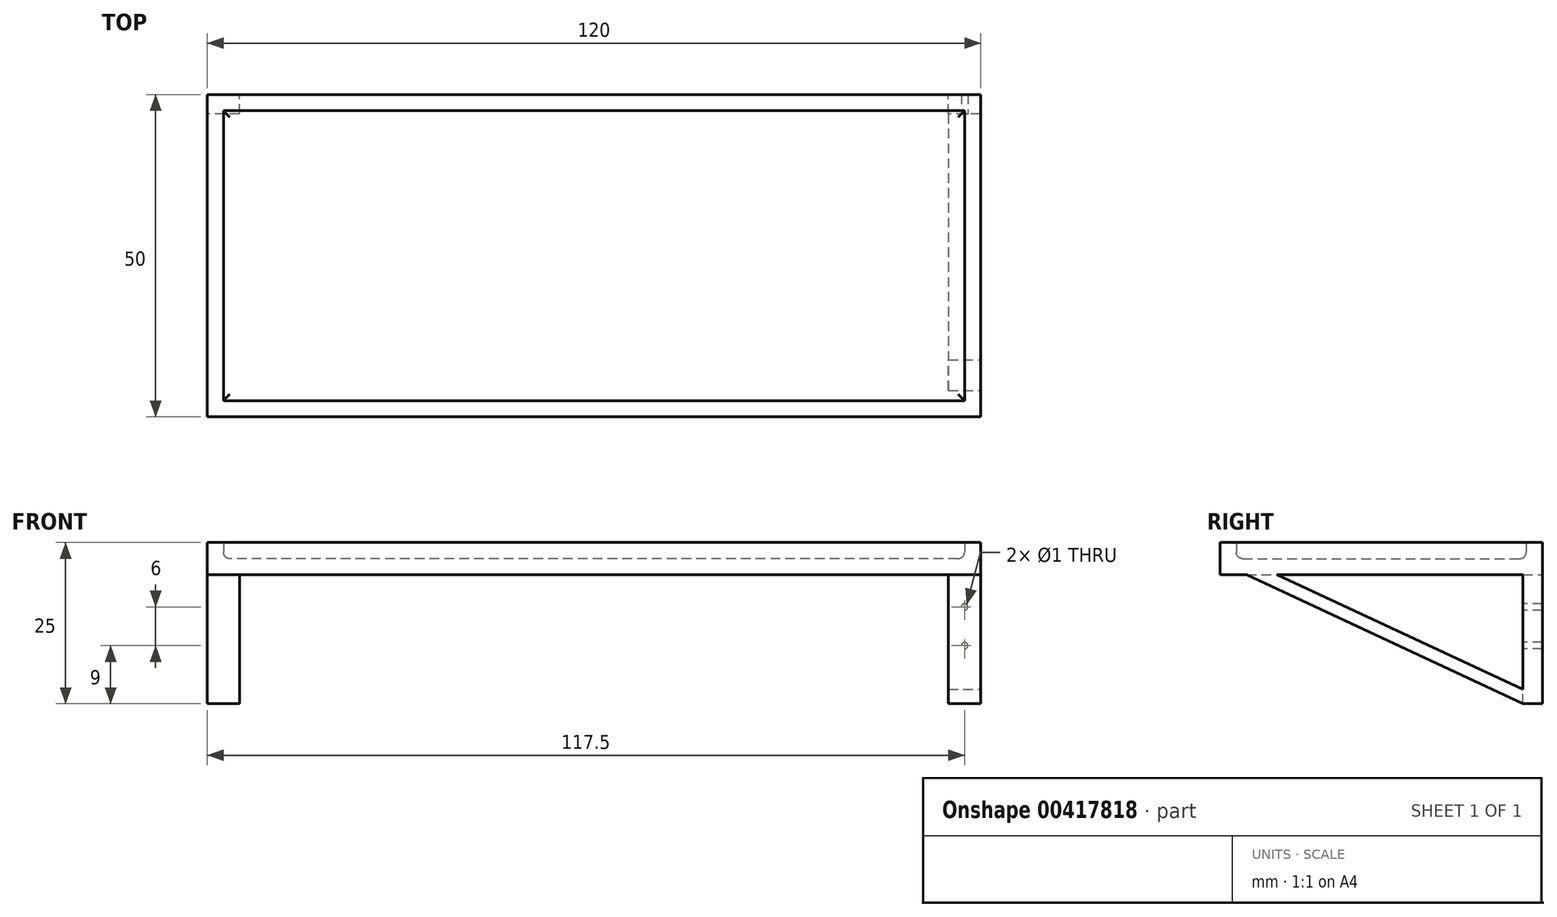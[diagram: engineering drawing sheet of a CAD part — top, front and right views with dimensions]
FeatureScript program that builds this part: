
annotation { "Feature Type Name" : "Feature", "Feature Type Description" : "" }
export const myFeature = defineFeature(function(context is Context, id is Id, definition is map)
    precondition{}
    {
        {
            var Q0;
            Q0=qCreatedBy(makeId("Top.planeOp"),FACE);
            var sketch = newSketch(context, id + "F0", { "sketchPlane" : qUnion([Q0])});
            skLineSegment(sketch, "E0.bottom", {"start": v(60, -50) * mm, "end": v(-60, -50) * mm});
            skLineSegment(sketch, "E0.top", {"start": v(60, 0) * mm, "end": v(-60, 0) * mm});
            skLineSegment(sketch, "E0.left", {"start": v(60, -50) * mm, "end": v(60, 0) * mm});
            skLineSegment(sketch, "E0.right", {"start": v(-60, -50) * mm, "end": v(-60, 0) * mm});
            skPoint(sketch, "E0.middle", {"position": v(0, 0) * mm});
            skSolve(sketch);
        }
        {
            var Q0;
            Q0=makeQuery(id+"F0.imprint","IMPRINT",FACE,{"disambiguationData":[TD([[makeQuery(id+"F0.imprint","IMPRINT",EDGE,{"derivedFrom":sQuery(id+"F0.wireOp",EDGE,"E0.bottom")}),-1.0]])]});
            extrude(context, id + "F1", {"entities" : qUnion([Q0]), "depth" : 5 * mm});
        }
        {
            var Q0;
            Q0=makeQuery(id+"F1.opExtrude","CAP_FACE",FACE,{"disambiguationData":[OSD([sQuery(id+"F0.wireOp",EDGE,"E0.bottom"),sQuery(id+"F0.wireOp",EDGE,"E0.top"),sQuery(id+"F0.wireOp",EDGE,"E0.left"),sQuery(id+"F0.wireOp",EDGE,"E0.right")])],"isStart":false});
            shell(context, id + "F2", {"entities" : qUnion([Q0]), "thickness" : 2.5 * mm});
        }
        {
            var Q0;
            Q0=makeQuery(id+"F1.opExtrude","SWEPT_FACE",FACE,{"disambiguationData":[OSD([sQuery(id+"F0.wireOp",EDGE,"E0.top")])]});
            var sketch = newSketch(context, id + "F3", { "sketchPlane" : qUnion([Q0])});
            skPoint(sketch, "E1.0", {"position": v(-60, 5) * mm});
            skLineSegment(sketch, "E2.0", {"start": v(-60, 5) * mm, "end": v(60, 5) * mm});
            skPoint(sketch, "E3.0", {"position": v(-60, 0) * mm});
            skLineSegment(sketch, "E4.0", {"start": v(-60, 0) * mm, "end": v(60, 0) * mm});
            skLineSegment(sketch, "E5", {"start": v(-60, 5) * mm, "end": v(-60, -20) * mm});
            skLineSegment(sketch, "E6", {"start": v(-60, -20) * mm, "end": v(-55, -20) * mm});
            skLineSegment(sketch, "E7", {"start": v(-55, -20) * mm, "end": v(-55, 0) * mm});
            skLineSegment(sketch, "E8.MirrorCS", {"start": v(55, -20) * mm, "end": v(55, 0) * mm});
            skLineSegment(sketch, "E9.MirrorCS", {"start": v(60, 5) * mm, "end": v(60, -20) * mm});
            skLineSegment(sketch, "E10.MirrorCS", {"start": v(60, -20) * mm, "end": v(55, -20) * mm});
            skSolve(sketch);
        }
        {
            var Q0;
            {var subQ4=sQuery(id+"F3.wireOp",EDGE,"E6");Q0=makeQuery(id+"F3.imprint","IMPRINT",FACE,{"disambiguationData":[TD([[makeQuery(id+"F3.imprint","IMPRINT",EDGE,{"derivedFrom":subQ4}),1.0]])]});}
            var Q1;
            {var subQ3=sQuery(id+"F3.wireOp",EDGE,"E8.MirrorCS");Q1=makeQuery(id+"F3.imprint","IMPRINT",FACE,{"disambiguationData":[TD([[makeQuery(id+"F3.imprint","IMPRINT",EDGE,{"derivedFrom":subQ3}),-1.0]])]});}
            extrude(context, id + "F4", {"entities" : qUnion([Q0, Q1]), "operationType" : NewBodyOperationType.ADD, "oppositeDirection" : true, "depth" : 3 * mm});
        }
        {
            var Q0;
            Q0=makeQuery(id+"F4.boolean.opBoolean","MERGE",FACE,{"derivedFrom":[makeQuery(id+"F1.opExtrude","SWEPT_FACE",FACE,{"disambiguationData":[OSD([sQuery(id+"F0.wireOp",EDGE,"E0.left")])]}),makeQuery(id+"F4.opExtrude","SWEPT_FACE",FACE,{"disambiguationData":[OSD([sQuery(id+"F3.wireOp",EDGE,"E5")])]})]});
            var sketch = newSketch(context, id + "F5", { "sketchPlane" : qUnion([Q0])});
            skLineSegment(sketch, "E11.0", {"start": v(-50, 0) * mm, "end": v(-3, 0) * mm});
            skPoint(sketch, "E12.0", {"position": v(-3, -20) * mm});
            skLineSegment(sketch, "E13", {"start": v(-3, -20) * mm, "end": v(-45.9, 0) * mm});
            skLineSegment(sketch, "E14.0", {"start": v(-2.15, -18.19) * mm, "end": v(-45.04, 1.81) * mm});
            skSolve(sketch);
        }
        {
            var Q0;
            {var subQ0=sQuery(id+"F5.wireOp",EDGE,"E13");Q0=makeQuery(id+"F5.imprint","IMPRINT",FACE,{"disambiguationData":[TD([[makeQuery(id+"F5.imprint","IMPRINT",EDGE,{"derivedFrom":subQ0}),-1.0]])]});}
            extrude(context, id + "F6", {"entities" : qUnion([Q0]), "operationType" : NewBodyOperationType.ADD, "oppositeDirection" : true, "depth" : 5 * mm});
        }
        {
            var Q0;
            Q0=makeQuery(id+"F4.opExtrude","CAP_FACE",FACE,{"disambiguationData":[OSD([sQuery(id+"F3.wireOp",EDGE,"E4.0"),sQuery(id+"F3.wireOp",EDGE,"E5"),sQuery(id+"F3.wireOp",EDGE,"E6"),sQuery(id+"F3.wireOp",EDGE,"E7")])],"isStart":false});
            var sketch = newSketch(context, id + "F7", { "sketchPlane" : qUnion([Q0])});
            skPoint(sketch, "E15", {"position": v(57.5, -5) * mm});
            skPoint(sketch, "E16", {"position": v(57.5, -11) * mm});
            skSolve(sketch);
        }
        {
            var Q0;
            Q0=sQuery(id+"F7.wireOp",VERTEX,"E15");
            var Q1;
            Q1=sQuery(id+"F7.wireOp",VERTEX,"E16");
            var Q2;
            Q2=makeQuery(id+"F1.opExtrude","SWEPT_BODY",BODY,{"disambiguationData":[OSD([sQuery(id+"F0.wireOp",EDGE,"E0.bottom"),sQuery(id+"F0.wireOp",EDGE,"E0.top"),sQuery(id+"F0.wireOp",EDGE,"E0.left"),sQuery(id+"F0.wireOp",EDGE,"E0.right")])]});
            hole(context, id + "F8", {"style" : HoleStyle.SIMPLE, "endStyle" : HoleEndStyle.BLIND, "holeDiameter" : 1 * mm, "holeDepth" : 20 * mm, "isTappedThrough" : true, "tappedDepth" : 19.25 * mm, "tapClearance" : 3, "startFromSketch" : true, "locations" : qUnion([Q0, Q1]), "scope" : qUnion([Q2])});
        }
        {
            var Q0;
            Q0=makeQuery(id+"F2.opShell","OFFSET_FACE",FACE,{"disambiguationData":[OSD([sQuery(id+"F0.wireOp",EDGE,"E0.bottom"),sQuery(id+"F0.wireOp",EDGE,"E0.top"),sQuery(id+"F0.wireOp",EDGE,"E0.left"),sQuery(id+"F0.wireOp",EDGE,"E0.right")])]});
            fillet(context, id + "F9", {"entities" : qUnion([Q0]), "radius" : 1 * mm, "tangentPropagation" : true, "allowEdgeOverflow" : false});
        }
    });
